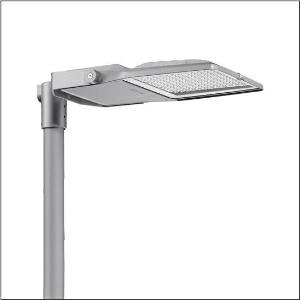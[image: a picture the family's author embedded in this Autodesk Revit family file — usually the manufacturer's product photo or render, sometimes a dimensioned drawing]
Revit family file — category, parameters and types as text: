
# Revit family: floodlight_fl_21_iq_midi___pl52_5xa7782f4d3a_fe87
name_source: partatom
category: Lighting Fixtures
units: mm (PartAtom-declared; Revit-internal decimal feet)

## family parameters
Cut with Voids When Loaded = No
Host = Face
Light Source = No
Part Type = Normal
Room Calculation Point = No
Round Connector Dimension = Use Diameter
Shared = No

## types (1)
- --- (1 x LED, 37330 lm, 270.2 W, 4000K)
    Apparent Load = 270 VA
    CIE Flux Codes = 26 60 98 100 100
    Color Rendering = 70
    Color Temperature = 4000K
    Default Elevation = 1800 mm
    Description = Floodlight FL 21 iQ midi, floodlight, primary light control with lens, of PMMA, primary optical cover: protective disc, of toughened safety glass, transparent, light distribution: PL52, light emission: direct distribution, installation type: surface-mounted, LED, High Power LED, rated luminous flux: 37.330lm, luminous efficacy: 138lm/W, light colour: 740, colour temperature: 4000K, control gear: ECG iQ, control: optimised constant luminous flux control (CLO 2.0), Desk-Remote (wireless, voltage-free reading and setting of iQ features in the workshop via application-optimized NFC function/RFID function), Smart-Wire, Night-Set, Temp-Guard, Auto-Match, Street-Remote, with terminal, 6-pole, mains connection: 220..240V, AC, 50/60Hz, start of lifetime: 270W, end of service life: 287W, reduction: 118W, luminaire housing, of diecast aluminium, powder-coated, Siteco® metallic grey (DB 702S), corrosivity category C5 mid according to DIN EN ISO 12944, sealing non-destructively replaceable, please order mast flange separately, mast bracket, of steel, galvanised, powder-coated, Siteco® metallic grey (DB 702S), protection rating (complete): IP66, insulation class (complete): insulation class II (safety insulation), certification: CE, protection symbol: D, impact resistance: IK08, permissible operating ambient temperature: -40..+40°C, permissible operating ambient temperature for outdoor applications: -40..+50°C, standard: DIN EN 12944, LABS conformity tested according to VDMA 24364:2018-05, packaging unit: 1 piece

Light Distribution: PL52
    Height = 76 mm
    Lamp = 1 x LED
    Lamp Light Flux = 37330 lm
    Lamp Power = 270.2 W
    Lamp count = 1
    Length = 657 mm
    Luminous efficacy = 138 lm/W
    Manufacturer = Siteco
    ModVariant = No
    Model = 5XA7782F4D3A
    Number of Poles = 1
    OnlyDefault = Yes
    Power Factor = 1
    Product Name = Floodlight FL 21 iQ midi | PL52
    Product group = floodlight | pylon annexe
    ProductGroupID = 6200
    Protection Class = Protection class II
    Protection Degree = IP 66
    RLX_Detail_Level = 1
    RLX_Emergency_Light_Flux = 0 lm
    RLX_Emergency_Type = 0
    RLX_Emergency_Type_DB = No
    RlxData = <blob elided: 153841 chars, md5=32f27694>
    Socket = socket
    Standby Power = 0 W
    System Light Flux = 37330 lm
    System Power = 270 W
    Type Comments = factory setting: luminous flux: 100 % | dim-lin: 254 | 620 mA
    Type Image = l_1007123.jpg
    URL = http://relux.com
    VarID = @adj_035649
    Voltage = 0 V
    Weight = 0.00 kg
    Width = 442 mm

## geometry (parser evidence)
native form markers: Blend x4, Sweep x12
no freeform markers — native parametric forms only
